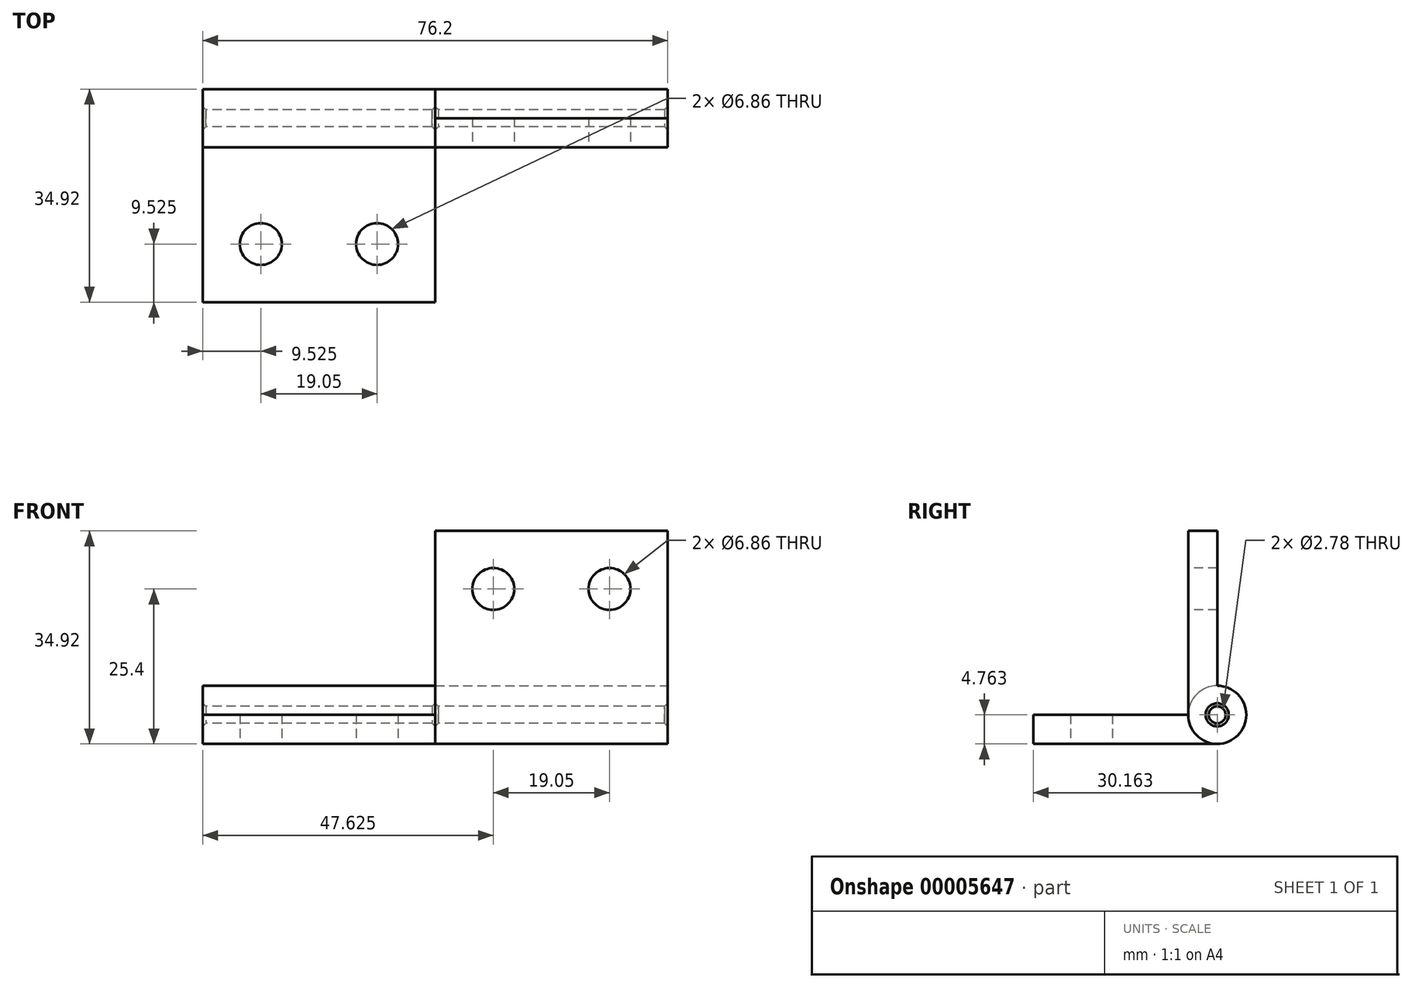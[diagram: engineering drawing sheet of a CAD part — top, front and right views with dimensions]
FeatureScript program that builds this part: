
annotation { "Feature Type Name" : "Feature", "Feature Type Description" : "" }
export const myFeature = defineFeature(function(context is Context, id is Id, definition is map)
    precondition{}
    {
        {
            var Q0;
            Q0=qCreatedBy(makeId("Top.planeOp"),FACE);
            var sketch = newSketch(context, id + "F0", { "sketchPlane" : qUnion([Q0])});
            skLineSegment(sketch, "E0.bottom", {"start": v(0, 0) * mm, "end": v(38.1, 0) * mm});
            skLineSegment(sketch, "E0.top", {"start": v(0, 25.4) * mm, "end": v(38.1, 25.4) * mm});
            skLineSegment(sketch, "E0.left", {"start": v(0, 0) * mm, "end": v(0, 25.4) * mm});
            skLineSegment(sketch, "E0.right", {"start": v(38.1, 0) * mm, "end": v(38.1, 25.4) * mm});
            skSolve(sketch);
        }
        {
            var Q0;
            Q0=makeQuery(id+"F0.imprint","IMPRINT",FACE,{"disambiguationData":[TD([[makeQuery(id+"F0.imprint","IMPRINT",EDGE,{"derivedFrom":sQuery(id+"F0.wireOp",EDGE,"E0.bottom")}),1.0]])]});
            extrude(context, id + "F1", {"entities" : qUnion([Q0]), "depth" : 4.76 * mm});
        }
        {
            var Q0;
            Q0=makeQuery(id+"F1.opExtrude","CAP_FACE",FACE,{"disambiguationData":[OSD([sQuery(id+"F0.wireOp",EDGE,"E0.bottom"),sQuery(id+"F0.wireOp",EDGE,"E0.top"),sQuery(id+"F0.wireOp",EDGE,"E0.left"),sQuery(id+"F0.wireOp",EDGE,"E0.right")])],"isStart":true});
            var sketch = newSketch(context, id + "F2", { "sketchPlane" : qUnion([Q0])});
            skCircle(sketch, "E1", {"center": v(9.53, -9.53) * mm, "radius": 4.76 * mm});
            skCircle(sketch, "E2", {"center": v(28.58, -9.53) * mm, "radius": 4.76 * mm});
            skCircle(sketch, "E3", {"center": v(9.53, -9.53) * mm, "radius": 3.43 * mm});
            skCircle(sketch, "E4", {"center": v(28.58, -9.53) * mm, "radius": 3.43 * mm});
            skSolve(sketch);
        }
        {
            var Q0;
            Q0=makeQuery(id+"F2.imprint","IMPRINT",FACE,{"disambiguationData":[TD([[makeQuery(id+"F2.imprint","IMPRINT",EDGE,{"derivedFrom":sQuery(id+"F2.wireOp",EDGE,"E3")}),1.0]])]});
            var Q1;
            Q1=makeQuery(id+"F2.imprint","IMPRINT",FACE,{"disambiguationData":[TD([[makeQuery(id+"F2.imprint","IMPRINT",EDGE,{"derivedFrom":sQuery(id+"F2.wireOp",EDGE,"E4")}),1.0]])]});
            var Q2;
            Q2=makeQuery(id+"F1.opExtrude","CAP_FACE",FACE,{"disambiguationData":[OSD([sQuery(id+"F0.wireOp",EDGE,"E0.bottom"),sQuery(id+"F0.wireOp",EDGE,"E0.top"),sQuery(id+"F0.wireOp",EDGE,"E0.left"),sQuery(id+"F0.wireOp",EDGE,"E0.right")])],"isStart":false});
            extrude(context, id + "F3", {"entities" : qUnion([Q0, Q1]), "operationType" : NewBodyOperationType.REMOVE, "endBound" : BoundingType.UP_TO_SURFACE, "oppositeDirection" : true, "endBoundEntityFace" : qUnion([Q2]), "depth" : 25.4 * mm});
        }
        {
            var Q0;
            Q0=makeQuery(id+"F1.opExtrude","SWEPT_FACE",FACE,{"disambiguationData":[OSD([sQuery(id+"F0.wireOp",EDGE,"E0.left")])]});
            var sketch = newSketch(context, id + "F4", { "sketchPlane" : qUnion([Q0])});
            skCircle(sketch, "E5", {"center": v(-30.16, 4.76) * mm, "radius": 1.39 * mm});
            skCircle(sketch, "E6", {"center": v(-30.16, 4.76) * mm, "radius": 4.76 * mm});
            skLineSegment(sketch, "E7", {"start": v(-25.4, 0) * mm, "end": v(-30.16, 0) * mm});
            skSolve(sketch);
        }
        {
            var Q0;
            Q0=makeQuery(id+"F4.imprint","IMPRINT",FACE,{"disambiguationData":[TD([[makeQuery(id+"F4.imprint","IMPRINT",EDGE,{"derivedFrom":sQuery(id+"F4.wireOp",EDGE,"E5")}),-1.0]])]});
            var Q1;
            {var subQ2=sQuery(id+"F4.wireOp",EDGE,"E7");Q1=makeQuery(id+"F4.imprint","IMPRINT",FACE,{"disambiguationData":[TD([[makeQuery(id+"F4.imprint","IMPRINT",EDGE,{"derivedFrom":subQ2}),-1.0]])]});}
            var Q2;
            Q2=makeQuery(id+"F1.opExtrude","SWEPT_FACE",FACE,{"disambiguationData":[OSD([sQuery(id+"F0.wireOp",EDGE,"E0.right")])]});
            extrude(context, id + "F5", {"entities" : qUnion([Q0, Q1]), "operationType" : NewBodyOperationType.ADD, "endBound" : BoundingType.UP_TO_SURFACE, "oppositeDirection" : true, "endBoundEntityFace" : qUnion([Q2]), "depth" : 25.4 * mm});
        }
        {
            var Q0;
            Q0=makeQuery(id+"F5.opExtrude","CAP_EDGE",EDGE,{"disambiguationData":[OSD([sQuery(id+"F4.wireOp",EDGE,"E5")])],"isStart":false});
            var Q1;
            Q1=makeQuery(id+"F5.opExtrude","CAP_EDGE",EDGE,{"disambiguationData":[OSD([sQuery(id+"F4.wireOp",EDGE,"E5")])],"isStart":true});
            chamfer(context, id + "F6", {"entities" : qUnion([Q0, Q1]), "width" : 0.5 * mm, "tangentPropagation" : true});
        }
        {
            var Q0;
            Q0=makeQuery(id+"F1.opExtrude","SWEPT_BODY",BODY,{"disambiguationData":[OSD([sQuery(id+"F0.wireOp",EDGE,"E0.bottom"),sQuery(id+"F0.wireOp",EDGE,"E0.top"),sQuery(id+"F0.wireOp",EDGE,"E0.left"),sQuery(id+"F0.wireOp",EDGE,"E0.right")])]});
            var Q1;
            Q1=makeQuery(id+"F5.opExtrude","SWEPT_FACE",FACE,{"disambiguationData":[OSD([sQuery(id+"F4.wireOp",EDGE,"E5")])]});
            transform(context, id + "F7", {"entities" : qUnion([Q0]), "transformType" : TransformType.ROTATION, "transformAxis" : qUnion([Q1]), "angle" : 90 * degree, "oppositeDirection" : true, "makeCopy" : true});
        }
        {
            var Q0;
            Q0=makeQuery(id+"F7.opPattern","COPY",BODY,{"derivedFrom":makeQuery(id+"F1.opExtrude","SWEPT_BODY",BODY,{"disambiguationData":[OSD([sQuery(id+"F0.wireOp",EDGE,"E0.bottom"),sQuery(id+"F0.wireOp",EDGE,"E0.top"),sQuery(id+"F0.wireOp",EDGE,"E0.left"),sQuery(id+"F0.wireOp",EDGE,"E0.right")])]}),"instanceName":"1"});
            transform(context, id + "F8", {"entities" : qUnion([Q0]), "transformType" : TransformType.TRANSLATION_3D, "dx" : 38.1 * mm, "dy" : 0 * mm, "dz" : 0 * mm, "makeCopy" : false});
        }
    });
